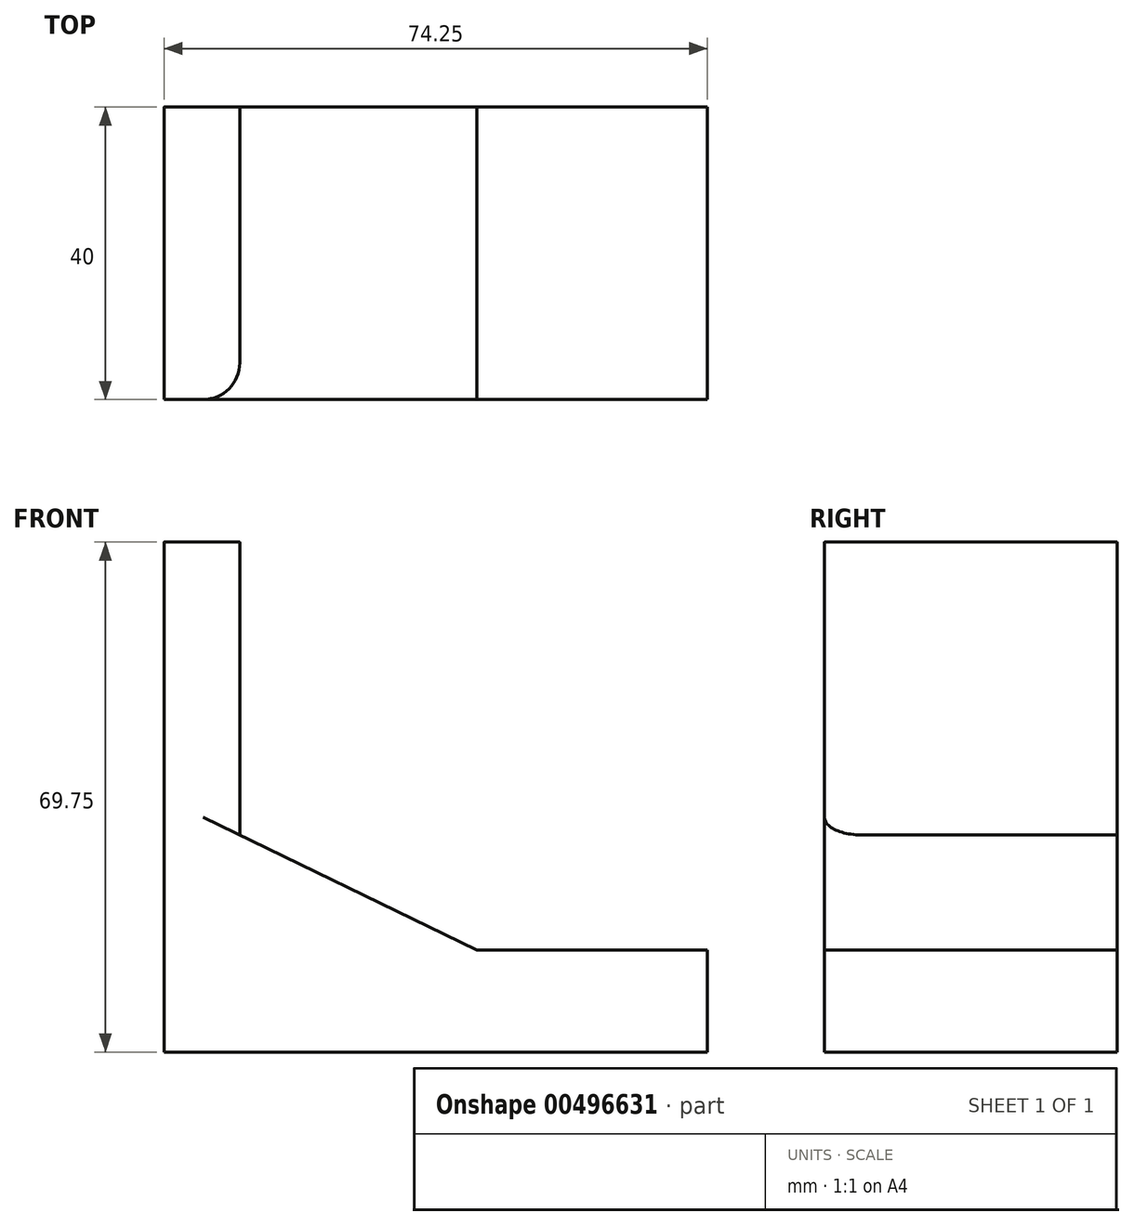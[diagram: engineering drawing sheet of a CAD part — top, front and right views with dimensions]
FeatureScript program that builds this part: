
annotation { "Feature Type Name" : "Feature", "Feature Type Description" : "" }
export const myFeature = defineFeature(function(context is Context, id is Id, definition is map)
    precondition{}
    {
        {
            var Q0;
            Q0=qCreatedBy(makeId("Front.planeOp"),FACE);
            var sketch = newSketch(context, id + "F0", { "sketchPlane" : qUnion([Q0])});
            skLineSegment(sketch, "E0", {"start": v(0, 0) * mm, "end": v(0, 40.05) * mm});
            skLineSegment(sketch, "E1", {"start": v(0, 40.05) * mm, "end": v(10.35, 40.05) * mm});
            skLineSegment(sketch, "E2", {"start": v(10.35, 40.05) * mm, "end": v(10.35, 0) * mm});
            skLineSegment(sketch, "E3", {"start": v(10.35, 0) * mm, "end": v(42.75, -15.75) * mm});
            skLineSegment(sketch, "E4", {"start": v(42.75, -15.75) * mm, "end": v(74.25, -15.75) * mm});
            skLineSegment(sketch, "E5", {"start": v(74.25, -15.75) * mm, "end": v(74.25, -29.7) * mm});
            skLineSegment(sketch, "E6", {"start": v(74.25, -29.7) * mm, "end": v(0, -29.7) * mm});
            skLineSegment(sketch, "E7", {"start": v(0, -29.7) * mm, "end": v(0, 0) * mm});
            skSolve(sketch);
        }
        {
            var Q0;
            Q0=makeQuery(id+"F0.imprint","IMPRINT",FACE,{"disambiguationData":[TD([[makeQuery(id+"F0.imprint","IMPRINT",EDGE,{"derivedFrom":sQuery(id+"F0.wireOp",EDGE,"E0")}),-1.0]])]});
            extrude(context, id + "F1", {"entities" : qUnion([Q0]), "depth" : 40 * mm});
        }
        {
            var Q0;
            Q0=makeQuery(id+"F1.opExtrude","SWEPT_FACE",FACE,{"disambiguationData":[OSD([sQuery(id+"F0.wireOp",EDGE,"E1")])]});
            var Q1;
            Q1=makeQuery(id+"F1.opExtrude","CAP_EDGE",EDGE,{"disambiguationData":[OSD([sQuery(id+"F0.wireOp",EDGE,"E1")])],"isStart":true});
            var Q2;
            Q2=makeQuery(id+"F1.opExtrude","SWEPT_EDGE",EDGE,{"disambiguationData":[OSD([sQuery(id+"F0.wireOp",EDGE,"E0"),sQuery(id+"F0.wireOp",EDGE,"E1")])]});
            fillet(context, id + "F2", {"entities" : qUnion([Q0, Q1, Q2]), "radius" : 0.02 * mm, "tangentPropagation" : true, "allowEdgeOverflow" : false});
        }
        {
            var Q0;
            Q0=makeQuery(id+"F1.opExtrude","SWEPT_FACE",FACE,{"disambiguationData":[OSD([sQuery(id+"F0.wireOp",EDGE,"E1")])]});
            var Q1;
            Q1=makeQuery(id+"F1.opExtrude","CAP_EDGE",EDGE,{"disambiguationData":[OSD([sQuery(id+"F0.wireOp",EDGE,"E2")])],"isStart":false});
            fillet(context, id + "F3", {"entities" : qUnion([Q0, Q1]), "radius" : 5 * mm, "tangentPropagation" : true, "allowEdgeOverflow" : false});
        }
    });
